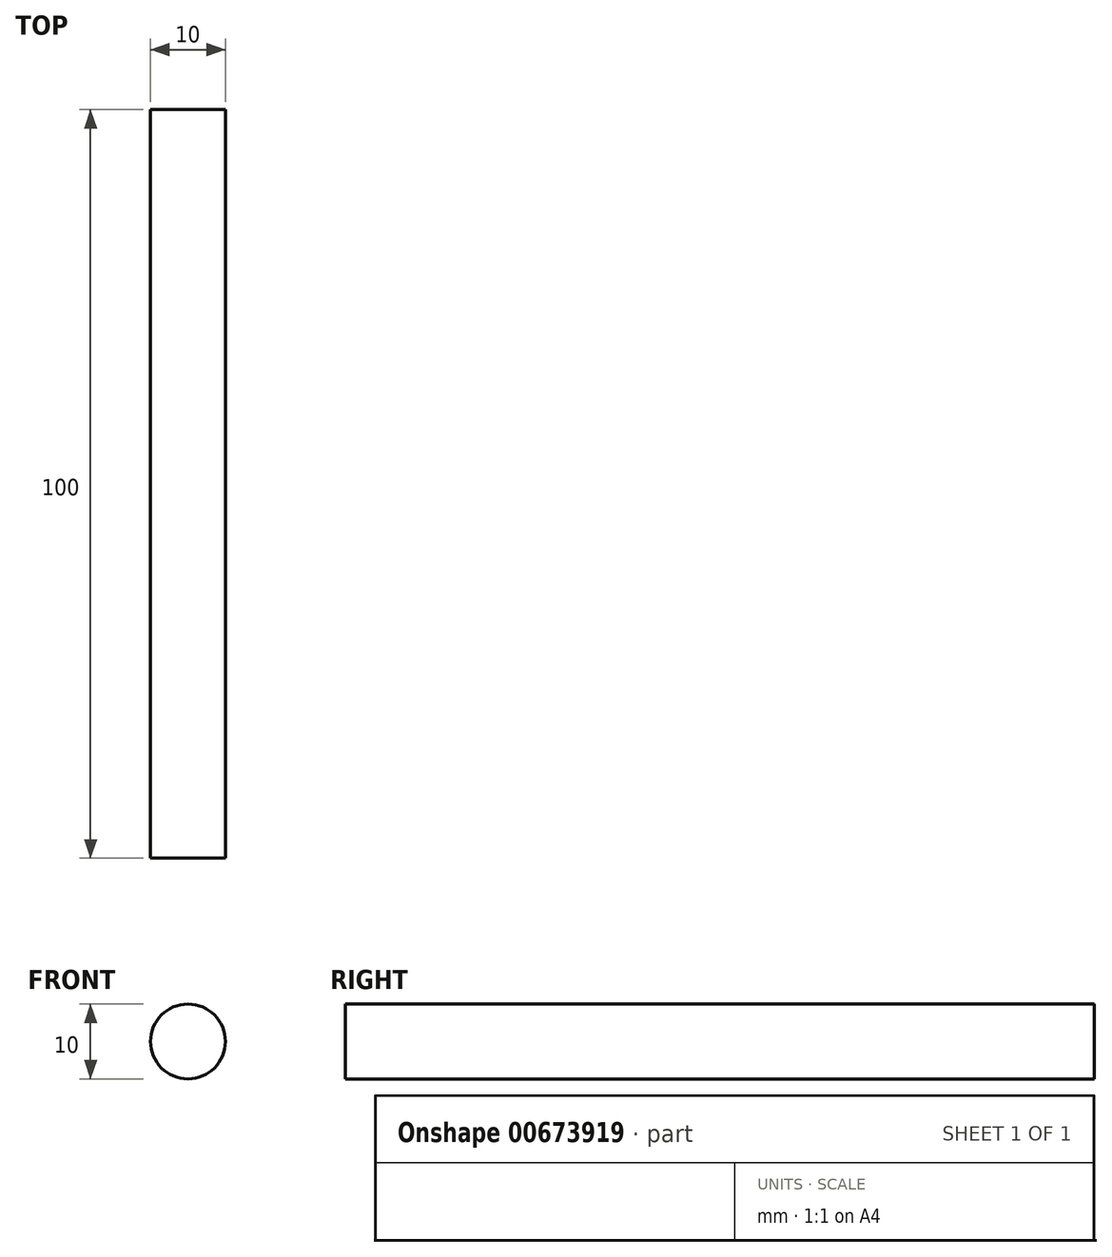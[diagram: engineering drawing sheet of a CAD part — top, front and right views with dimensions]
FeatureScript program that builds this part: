
annotation { "Feature Type Name" : "Feature", "Feature Type Description" : "" }
export const myFeature = defineFeature(function(context is Context, id is Id, definition is map)
    precondition{}
    {
        {
            var Q0;
            Q0=qCreatedBy(makeId("Front.planeOp"),FACE);
            var sketch = newSketch(context, id + "F0", { "sketchPlane" : qUnion([Q0])});
            skCircle(sketch, "E0", {"center": v(0, 0) * mm, "radius": 5 * mm});
            skSolve(sketch);
        }
        {
            var Q0;
            Q0 = qSketchRegion(id + "F0", true);
            extrude(context, id + "F1", {"entities" : qUnion([Q0]), "depth" : 100 * mm, "offsetDistance" : 25 * mm});
        }
    });
